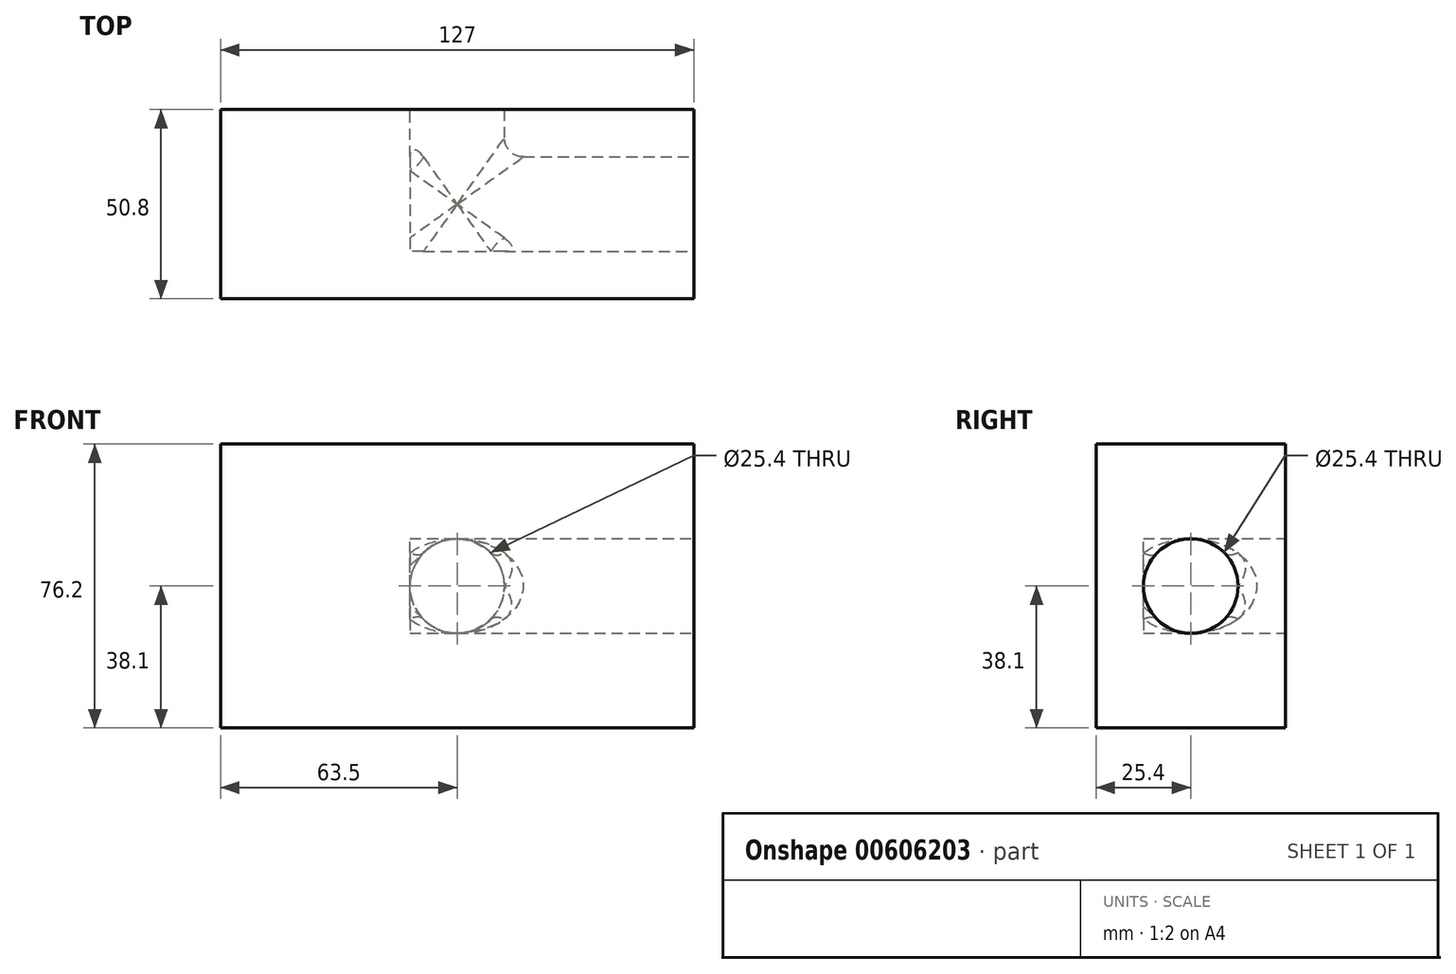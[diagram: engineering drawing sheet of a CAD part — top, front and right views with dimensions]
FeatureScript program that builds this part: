
annotation { "Feature Type Name" : "Feature", "Feature Type Description" : "" }
export const myFeature = defineFeature(function(context is Context, id is Id, definition is map)
    precondition{}
    {
        {
            var Q0;
            Q0=qCreatedBy(makeId("Front.planeOp"),FACE);
            var sketch = newSketch(context, id + "F0", { "sketchPlane" : qUnion([Q0])});
            skLineSegment(sketch, "E0.bottom", {"start": v(63.5, 38.1) * mm, "end": v(-63.5, 38.1) * mm});
            skLineSegment(sketch, "E0.top", {"start": v(63.5, -38.1) * mm, "end": v(-63.5, -38.1) * mm});
            skLineSegment(sketch, "E0.left", {"start": v(63.5, 38.1) * mm, "end": v(63.5, -38.1) * mm});
            skLineSegment(sketch, "E0.right", {"start": v(-63.5, 38.1) * mm, "end": v(-63.5, -38.1) * mm});
            skPoint(sketch, "E0.middle", {"position": v(0, 0) * mm});
            skSolve(sketch);
        }
        {
            var Q0;
            Q0 = qSketchRegion(id + "F0", true);
            extrude(context, id + "F1", {"entities" : qUnion([Q0]), "depth" : 50.8 * mm, "offsetDistance" : 25.4 * mm});
        }
        {
            var Q0;
            Q0=qCreatedBy(makeId("Front.planeOp"),FACE);
            var sketch = newSketch(context, id + "F2", { "sketchPlane" : qUnion([Q0])});
            skCircle(sketch, "E1", {"center": v(0, 0) * mm, "radius": 12.7 * mm});
            skSolve(sketch);
        }
        {
            var Q0;
            Q0 = qSketchRegion(id + "F2", true);
            extrude(context, id + "F3", {"entities" : qUnion([Q0]), "operationType" : NewBodyOperationType.REMOVE, "depth" : 38.1 * mm, "offsetDistance" : 25.4 * mm});
        }
        {
            var Q0;
            Q0=makeQuery(id+"F1.opExtrude","SWEPT_FACE",FACE,{"disambiguationData":[OSD([sQuery(id+"F0.wireOp",EDGE,"E0.left")])]});
            var sketch = newSketch(context, id + "F4", { "sketchPlane" : qUnion([Q0])});
            skCircle(sketch, "E2", {"center": v(-25.4, 0) * mm, "radius": 12.7 * mm});
            skSolve(sketch);
        }
        {
            var Q0;
            Q0=makeQuery(id+"F4.imprint","IMPRINT",FACE,{"disambiguationData":[TD([[makeQuery(id+"F4.imprint","IMPRINT",EDGE,{"derivedFrom":sQuery(id+"F4.wireOp",EDGE,"E2")}),1.0]])]});
            extrude(context, id + "F5", {"entities" : qUnion([Q0]), "operationType" : NewBodyOperationType.REMOVE, "oppositeDirection" : true, "depth" : 76.2 * mm, "offsetDistance" : 25.4 * mm});
        }
        {
            var Q0;
            Q0=makeQuery(id+"F5.boolean.opBoolean","INTERSECT",EDGE,{"disambiguationData":[OD(3.0)],"derivedFrom":[makeQuery(id+"F3.boolean.opBoolean","COPY",FACE,{"derivedFrom":makeQuery(id+"F3.opExtrude","SWEPT_FACE",FACE,{"disambiguationData":[OSD([sQuery(id+"F2.wireOp",EDGE,"E1")])]})}),makeQuery(id+"F5.opExtrude","SWEPT_FACE",FACE,{"disambiguationData":[OSD([sQuery(id+"F4.wireOp",EDGE,"E2")])]})]});
            var Q1;
            Q1=makeQuery(id+"F5.boolean.opBoolean","INTERSECT",EDGE,{"disambiguationData":[OD(0.0)],"derivedFrom":[makeQuery(id+"F3.boolean.opBoolean","COPY",FACE,{"derivedFrom":makeQuery(id+"F3.opExtrude","SWEPT_FACE",FACE,{"disambiguationData":[OSD([sQuery(id+"F2.wireOp",EDGE,"E1")])]})}),makeQuery(id+"F5.opExtrude","SWEPT_FACE",FACE,{"disambiguationData":[OSD([sQuery(id+"F4.wireOp",EDGE,"E2")])]})]});
            var Q2;
            Q2=makeQuery(id+"F5.boolean.opBoolean","INTERSECT",EDGE,{"disambiguationData":[OD(1.0)],"derivedFrom":[makeQuery(id+"F3.boolean.opBoolean","COPY",FACE,{"derivedFrom":makeQuery(id+"F3.opExtrude","SWEPT_FACE",FACE,{"disambiguationData":[OSD([sQuery(id+"F2.wireOp",EDGE,"E1")])]})}),makeQuery(id+"F5.opExtrude","SWEPT_FACE",FACE,{"disambiguationData":[OSD([sQuery(id+"F4.wireOp",EDGE,"E2")])]})]});
            var Q3;
            Q3=makeQuery(id+"F5.boolean.opBoolean","INTERSECT",EDGE,{"disambiguationData":[OD(4.0)],"derivedFrom":[makeQuery(id+"F3.boolean.opBoolean","COPY",FACE,{"derivedFrom":makeQuery(id+"F3.opExtrude","SWEPT_FACE",FACE,{"disambiguationData":[OSD([sQuery(id+"F2.wireOp",EDGE,"E1")])]})}),makeQuery(id+"F5.opExtrude","SWEPT_FACE",FACE,{"disambiguationData":[OSD([sQuery(id+"F4.wireOp",EDGE,"E2")])]})]});
            var Q4;
            Q4=makeQuery(id+"F5.boolean.opBoolean","INTERSECT",EDGE,{"disambiguationData":[OD(2.0)],"derivedFrom":[makeQuery(id+"F3.boolean.opBoolean","COPY",FACE,{"derivedFrom":makeQuery(id+"F3.opExtrude","SWEPT_FACE",FACE,{"disambiguationData":[OSD([sQuery(id+"F2.wireOp",EDGE,"E1")])]})}),makeQuery(id+"F5.opExtrude","SWEPT_FACE",FACE,{"disambiguationData":[OSD([sQuery(id+"F4.wireOp",EDGE,"E2")])]})]});
            var Q5;
            Q5=makeQuery(id+"F5.boolean.opBoolean","INTERSECT",EDGE,{"disambiguationData":[OD(6.0)],"derivedFrom":[makeQuery(id+"F3.boolean.opBoolean","COPY",FACE,{"derivedFrom":makeQuery(id+"F3.opExtrude","SWEPT_FACE",FACE,{"disambiguationData":[OSD([sQuery(id+"F2.wireOp",EDGE,"E1")])]})}),makeQuery(id+"F5.opExtrude","SWEPT_FACE",FACE,{"disambiguationData":[OSD([sQuery(id+"F4.wireOp",EDGE,"E2")])]})]});
            fillet(context, id + "F6", {"entities" : qUnion([Q0, Q1, Q2, Q3, Q4, Q5]), "radius" : 5.08 * mm, "tangentPropagation" : true, "allowEdgeOverflow" : false});
        }
    });
